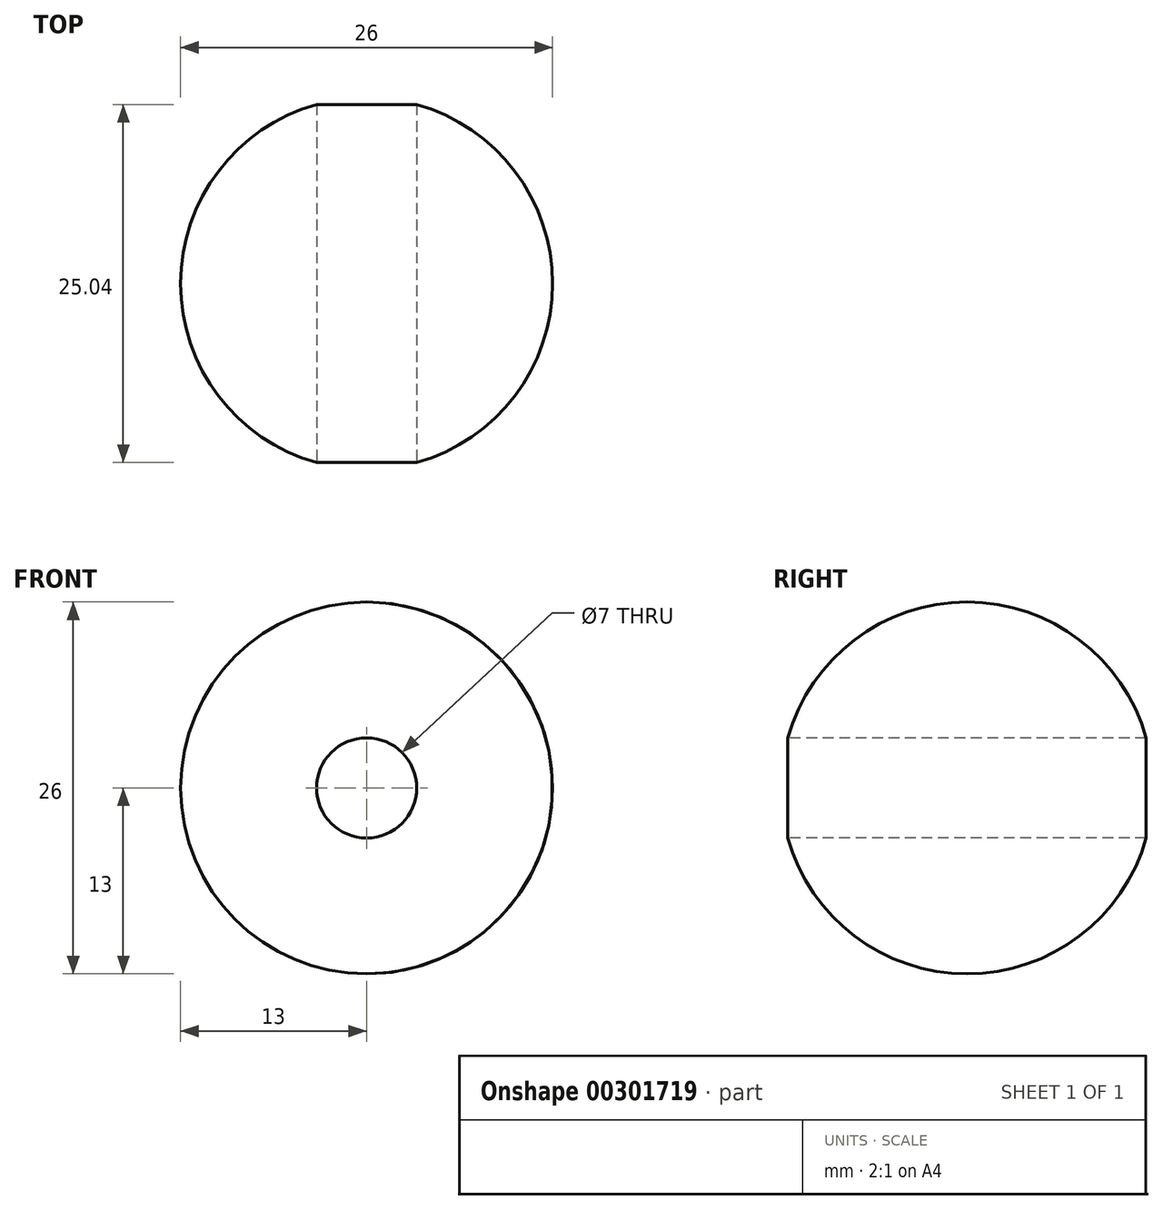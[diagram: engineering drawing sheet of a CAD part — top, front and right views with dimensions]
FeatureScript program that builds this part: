
annotation { "Feature Type Name" : "Feature", "Feature Type Description" : "" }
export const myFeature = defineFeature(function(context is Context, id is Id, definition is map)
    precondition{}
    {
        {
            var Q0;
            Q0=qCreatedBy(makeId("Front.planeOp"),FACE);
            var sketch = newSketch(context, id + "F0", { "sketchPlane" : qUnion([Q0])});
            skCircle(sketch, "E0", {"center": v(0, 0) * mm, "radius": 13 * mm});
            skLineSegment(sketch, "E1", {"start": v(0, 0) * mm, "end": v(0, 18.05) * mm});
            skLineSegment(sketch, "E2", {"start": v(0, 18.05) * mm, "end": v(0, -19.8) * mm});
            skSolve(sketch);
        }
        {
            var Q0;
            {var subQ0=sQuery(id+"F0.wireOp",EDGE,"E2");var subQ4=makeQuery(id+"F0.imprint","IMPRINT",VERTEX,{"derivedFrom":subQ0});Q0=makeQuery(id+"F0.imprint","IMPRINT",FACE,{"disambiguationData":[TD([[makeQuery(id+"F0.imprint","IMPRINT",EDGE,{"disambiguationData":[TD([[subQ4,1.0]])],"derivedFrom":subQ0}),1.0]])]});}
            var Q1;
            Q1=sQuery(id+"F0.wireOp",EDGE,"E2");
            revolve(context, id + "F1", {"entities" : qUnion([Q0]), "axis" : qUnion([Q1]), "revolveType" : RevolveType.FULL});
        }
        {
            var Q0;
            Q0=qCreatedBy(makeId("Front.planeOp"),FACE);
            cPlane(context, id + "F2", {"entities" : qUnion([Q0]), "cplaneType" : CPlaneType.OFFSET, "offset" : 48.5 * mm, "width" : 150 * mm, "height" : 150 * mm});
        }
        {
            var Q0;
            Q0=qCreatedBy(id+"F2.planeOp",FACE);
            var sketch = newSketch(context, id + "F3", { "sketchPlane" : qUnion([Q0])});
            skCircle(sketch, "E3", {"center": v(0, 0) * mm, "radius": 3.5 * mm});
            skSolve(sketch);
        }
        {
            var Q0;
            Q0=makeQuery(id+"F3.imprint","IMPRINT",FACE,{"disambiguationData":[TD([[makeQuery(id+"F3.imprint","IMPRINT",EDGE,{"derivedFrom":sQuery(id+"F3.wireOp",EDGE,"E3")}),1.0]])]});
            extrude(context, id + "F4", {"entities" : qUnion([Q0]), "operationType" : NewBodyOperationType.REMOVE, "oppositeDirection" : true, "depth" : 128.4 * mm});
        }
    });
